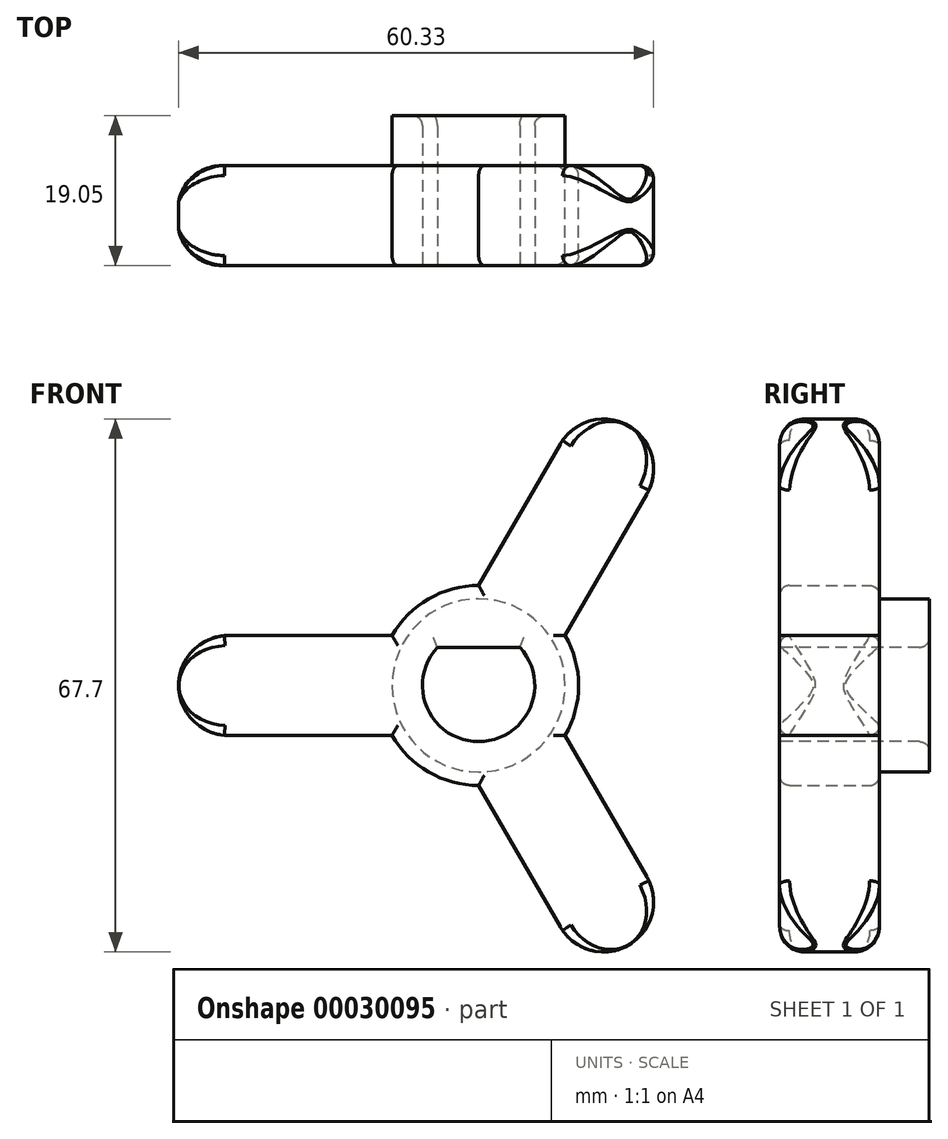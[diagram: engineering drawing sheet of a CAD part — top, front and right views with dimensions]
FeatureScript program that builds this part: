
annotation { "Feature Type Name" : "Feature", "Feature Type Description" : "" }
export const myFeature = defineFeature(function(context is Context, id is Id, definition is map)
    precondition{}
    {
        {
            var Q0;
            Q0=qCreatedBy(makeId("Front.planeOp"),FACE);
            var sketch = newSketch(context, id + "F0", { "sketchPlane" : qUnion([Q0])});
            skArc(sketch, "E0", {"start": v(-11, -6.35) * mm, "mid": v(-6.35, -11) * mm, "end": v(0, -12.7) * mm});
            skLineSegment(sketch, "E1", {"start": v(-12.7, 0) * mm, "end": v(-38.1, 0) * mm, "construction": true});
            skLineSegment(sketch, "E2", {"start": v(-11, 6.35) * mm, "end": v(-31.75, 6.35) * mm});
            skLineSegment(sketch, "E3", {"start": v(-38.1, 0) * mm, "end": v(-38.1, 0) * mm});
            skPoint(sketch, "E4.visualSharp", {"position": v(-38.1, 6.35) * mm});
            skArc(sketch, "E4.filletArc", {"start": v(-31.75, 6.35) * mm, "mid": v(-36.24, 4.5) * mm, "end": v(-38.1, 0) * mm});
            skLineSegment(sketch, "E5.MirrorCS", {"start": v(-11, -6.35) * mm, "end": v(-31.75, -6.35) * mm});
            skArc(sketch, "E6.MirrorCS", {"start": v(-31.75, -6.35) * mm, "mid": v(-36.24, -4.5) * mm, "end": v(-38.1, 0) * mm});
            skLineSegment(sketch, "E7.1.0", {"start": v(0, -12.7) * mm, "end": v(10.38, -30.67) * mm});
            skArc(sketch, "E7.1.1", {"start": v(10.38, -30.67) * mm, "mid": v(14.23, -33.63) * mm, "end": v(19.05, -33) * mm});
            skArc(sketch, "E7.1.2", {"start": v(21.37, -24.32) * mm, "mid": v(22, -29.14) * mm, "end": v(19.05, -33) * mm});
            skLineSegment(sketch, "E7.1.3", {"start": v(11, -6.35) * mm, "end": v(21.37, -24.32) * mm});
            skLineSegment(sketch, "E7.2.0", {"start": v(11, 6.35) * mm, "end": v(21.37, 24.32) * mm});
            skArc(sketch, "E7.2.1", {"start": v(21.37, 24.32) * mm, "mid": v(22, 29.14) * mm, "end": v(19.05, 33) * mm});
            skArc(sketch, "E7.2.2", {"start": v(10.38, 30.67) * mm, "mid": v(14.23, 33.63) * mm, "end": v(19.05, 33) * mm});
            skLineSegment(sketch, "E7.2.3", {"start": v(0, 12.7) * mm, "end": v(10.38, 30.67) * mm});
            skArc(sketch, "E8.trimOffspring", {"start": v(0, 12.7) * mm, "mid": v(-6.35, 11) * mm, "end": v(-11, 6.35) * mm});
            skArc(sketch, "E9.trimOffspring", {"start": v(11, -6.35) * mm, "mid": v(12.7, 0) * mm, "end": v(11, 6.35) * mm});
            skSolve(sketch);
        }
        {
            var Q0;
            Q0=makeQuery(id+"F0.imprint","IMPRINT",FACE,{"disambiguationData":[TD([[makeQuery(id+"F0.imprint","IMPRINT",EDGE,{"derivedFrom":sQuery(id+"F0.wireOp",EDGE,"E0")}),1.0]])]});
            extrude(context, id + "F1", {"entities" : qUnion([Q0]), "depth" : 19.05 * mm});
        }
        {
            var Q0;
            Q0=makeQuery(id+"F1.opExtrude","CAP_FACE",FACE,{"disambiguationData":[OSD([sQuery(id+"F0.wireOp",EDGE,"E0"),sQuery(id+"F0.wireOp",EDGE,"E2"),sQuery(id+"F0.wireOp",EDGE,"E4.filletArc"),sQuery(id+"F0.wireOp",EDGE,"E5.MirrorCS"),sQuery(id+"F0.wireOp",EDGE,"E6.MirrorCS"),sQuery(id+"F0.wireOp",EDGE,"E7.1.0"),sQuery(id+"F0.wireOp",EDGE,"E7.1.1"),sQuery(id+"F0.wireOp",EDGE,"E7.1.2"),sQuery(id+"F0.wireOp",EDGE,"E7.1.3"),sQuery(id+"F0.wireOp",EDGE,"E7.2.0"),sQuery(id+"F0.wireOp",EDGE,"E7.2.1"),sQuery(id+"F0.wireOp",EDGE,"E7.2.2"),sQuery(id+"F0.wireOp",EDGE,"E7.2.3"),sQuery(id+"F0.wireOp",EDGE,"E8.trimOffspring"),sQuery(id+"F0.wireOp",EDGE,"E9.trimOffspring")])],"isStart":false});
            var sketch = newSketch(context, id + "F2", { "sketchPlane" : qUnion([Q0])});
            skArc(sketch, "E10", {"start": v(-5.24, 4.85) * mm, "mid": v(0, -7.14) * mm, "end": v(5.24, 4.85) * mm});
            skLineSegment(sketch, "E11", {"start": v(-5.24, 4.85) * mm, "end": v(5.24, 4.85) * mm});
            skSolve(sketch);
        }
        {
            var Q0;
            Q0=makeQuery(id+"F2.imprint","IMPRINT",FACE,{"disambiguationData":[TD([[makeQuery(id+"F2.imprint","IMPRINT",EDGE,{"derivedFrom":sQuery(id+"F2.wireOp",EDGE,"E10")}),1.0]])]});
            extrude(context, id + "F3", {"entities" : qUnion([Q0]), "operationType" : NewBodyOperationType.REMOVE, "endBound" : BoundingType.THROUGH_ALL, "oppositeDirection" : true, "depth" : 25.4 * mm});
        }
        {
            var Q0;
            Q0=qCreatedBy(makeId("Top.planeOp"),FACE);
            var sketch = newSketch(context, id + "F4", { "sketchPlane" : qUnion([Q0])});
            skLineSegment(sketch, "E12", {"start": v(-38.18, -12.7) * mm, "end": v(-11, -12.7) * mm, "construction": true});
            skLineSegment(sketch, "E13", {"start": v(-11, -19.05) * mm, "end": v(-32.59, -19.05) * mm});
            skArc(sketch, "E14", {"start": v(-38.18, -12.7) * mm, "mid": v(-36.82, -17.14) * mm, "end": v(-32.59, -19.05) * mm});
            skLineSegment(sketch, "E15.MirrorCS", {"start": v(-11, -6.35) * mm, "end": v(-32.59, -6.35) * mm});
            skArc(sketch, "E16.MirrorCS", {"start": v(-38.18, -12.7) * mm, "mid": v(-36.82, -8.26) * mm, "end": v(-32.59, -6.35) * mm});
            skLineSegment(sketch, "E17", {"start": v(-11, -19.05) * mm, "end": v(-11, -6.35) * mm});
            skLineSegment(sketch, "E18", {"start": v(-11, -6.35) * mm, "end": v(-11, 0) * mm});
            skLineSegment(sketch, "E19", {"start": v(-11, 0) * mm, "end": v(-38.18, 0) * mm});
            skLineSegment(sketch, "E20", {"start": v(-38.18, 0) * mm, "end": v(-38.18, -12.7) * mm});
            skLineSegment(sketch, "E21.MirrorCS", {"start": v(-11, -19.05) * mm, "end": v(-11, -25.4) * mm});
            skLineSegment(sketch, "E22.MirrorCS", {"start": v(-38.18, -25.4) * mm, "end": v(-38.18, -12.7) * mm});
            skLineSegment(sketch, "E23.MirrorCS", {"start": v(-11, -25.4) * mm, "end": v(-38.18, -25.4) * mm});
            skSolve(sketch);
        }
        {
            var Q0;
            Q0=qCreatedBy(makeId("Right.planeOp"),FACE);
            var sketch = newSketch(context, id + "F5", { "sketchPlane" : qUnion([Q0])});
            skLineSegment(sketch, "E24", {"start": v(-63.5, 0) * mm, "end": v(63.5, 0) * mm, "construction": true});
            skSolve(sketch);
        }
        {
            var Q0;
            {var subQ4=sQuery(id+"F4.wireOp",EDGE,"E13");Q0=makeQuery(id+"F4.imprint","IMPRINT",FACE,{"disambiguationData":[TD([[makeQuery(id+"F4.imprint","IMPRINT",EDGE,{"derivedFrom":subQ4}),1.0]])]});}
            var Q1;
            {var subQ4=sQuery(id+"F4.wireOp",EDGE,"E15.MirrorCS");Q1=makeQuery(id+"F4.imprint","IMPRINT",FACE,{"disambiguationData":[TD([[makeQuery(id+"F4.imprint","IMPRINT",EDGE,{"derivedFrom":subQ4}),-1.0]])]});}
            var Q2;
            Q2 = qConstructionFilter(qBodyType(qCreatedBy(id + "F5" ,EDGE), BodyType.WIRE), ConstructionObject.NO);
            var Q3;
            Q3=sQuery(id+"F5.wireOp",EDGE,"E24");
            revolve(context, id + "F6", {"operationType" : NewBodyOperationType.REMOVE, "entities" : qUnion([Q0, Q1]), "surfaceEntities" : qUnion([Q2]), "axis" : qUnion([Q3]), "revolveType" : RevolveType.FULL, "oppositeDirection" : true});
        }
        {
            var Q0;
            Q0=makeQuery(id+"F6.boolean.opBoolean","COPY",EDGE,{"derivedFrom":makeQuery(id+"F6.opRevolve","SWEPT_EDGE",EDGE,{"disambiguationData":[OSD([sQuery(id+"F4.wireOp",EDGE,"E18"),sQuery(id+"F4.wireOp",EDGE,"E19")])]})});
            var Q1;
            Q1=makeQuery(id+"F3.boolean.opBoolean","INTERSECT",EDGE,{"derivedFrom":[makeQuery(id+"F1.opExtrude","CAP_FACE",FACE,{"disambiguationData":[OSD([sQuery(id+"F0.wireOp",EDGE,"E0"),sQuery(id+"F0.wireOp",EDGE,"E2"),sQuery(id+"F0.wireOp",EDGE,"E4.filletArc"),sQuery(id+"F0.wireOp",EDGE,"E5.MirrorCS"),sQuery(id+"F0.wireOp",EDGE,"E6.MirrorCS"),sQuery(id+"F0.wireOp",EDGE,"E7.1.0"),sQuery(id+"F0.wireOp",EDGE,"E7.1.1"),sQuery(id+"F0.wireOp",EDGE,"E7.1.2"),sQuery(id+"F0.wireOp",EDGE,"E7.1.3"),sQuery(id+"F0.wireOp",EDGE,"E7.2.0"),sQuery(id+"F0.wireOp",EDGE,"E7.2.1"),sQuery(id+"F0.wireOp",EDGE,"E7.2.2"),sQuery(id+"F0.wireOp",EDGE,"E7.2.3"),sQuery(id+"F0.wireOp",EDGE,"E8.trimOffspring"),sQuery(id+"F0.wireOp",EDGE,"E9.trimOffspring")])],"isStart":true}),makeQuery(id+"F3.opExtrude","SWEPT_FACE",FACE,{"disambiguationData":[OSD([sQuery(id+"F2.wireOp",EDGE,"E11")])]})]});
            var Q2;
            Q2=makeQuery(id+"F3.boolean.opBoolean","INTERSECT",EDGE,{"derivedFrom":[makeQuery(id+"F1.opExtrude","CAP_FACE",FACE,{"disambiguationData":[OSD([sQuery(id+"F0.wireOp",EDGE,"E0"),sQuery(id+"F0.wireOp",EDGE,"E2"),sQuery(id+"F0.wireOp",EDGE,"E4.filletArc"),sQuery(id+"F0.wireOp",EDGE,"E5.MirrorCS"),sQuery(id+"F0.wireOp",EDGE,"E6.MirrorCS"),sQuery(id+"F0.wireOp",EDGE,"E7.1.0"),sQuery(id+"F0.wireOp",EDGE,"E7.1.1"),sQuery(id+"F0.wireOp",EDGE,"E7.1.2"),sQuery(id+"F0.wireOp",EDGE,"E7.1.3"),sQuery(id+"F0.wireOp",EDGE,"E7.2.0"),sQuery(id+"F0.wireOp",EDGE,"E7.2.1"),sQuery(id+"F0.wireOp",EDGE,"E7.2.2"),sQuery(id+"F0.wireOp",EDGE,"E7.2.3"),sQuery(id+"F0.wireOp",EDGE,"E8.trimOffspring"),sQuery(id+"F0.wireOp",EDGE,"E9.trimOffspring")])],"isStart":true}),makeQuery(id+"F3.opExtrude","SWEPT_FACE",FACE,{"disambiguationData":[OSD([sQuery(id+"F2.wireOp",EDGE,"E10")])]})]});
            var Q3;
            Q3=makeQuery(id+"F3.boolean.opBoolean","COPY",EDGE,{"derivedFrom":makeQuery(id+"F3.opExtrude","CAP_EDGE",EDGE,{"disambiguationData":[OSD([sQuery(id+"F2.wireOp",EDGE,"E10")])],"isStart":true})});
            var Q4;
            Q4=makeQuery(id+"F1.opExtrude","CAP_EDGE",EDGE,{"disambiguationData":[OSD([sQuery(id+"F0.wireOp",EDGE,"E0")])],"isStart":false});
            var Q5;
            Q5=makeQuery(id+"F1.opExtrude","CAP_EDGE",EDGE,{"disambiguationData":[OSD([sQuery(id+"F0.wireOp",EDGE,"E5.MirrorCS")])],"isStart":false});
            var Q6;
            Q6=makeQuery(id+"F1.opExtrude","CAP_EDGE",EDGE,{"disambiguationData":[OSD([sQuery(id+"F0.wireOp",EDGE,"E7.1.0")])],"isStart":false});
            var Q7;
            Q7=makeQuery(id+"F1.opExtrude","CAP_EDGE",EDGE,{"disambiguationData":[OSD([sQuery(id+"F0.wireOp",EDGE,"E7.1.3")])],"isStart":false});
            var Q8;
            Q8=makeQuery(id+"F1.opExtrude","CAP_EDGE",EDGE,{"disambiguationData":[OSD([sQuery(id+"F0.wireOp",EDGE,"E9.trimOffspring")])],"isStart":false});
            var Q9;
            Q9=makeQuery(id+"F3.boolean.opBoolean","COPY",EDGE,{"derivedFrom":makeQuery(id+"F3.opExtrude","CAP_EDGE",EDGE,{"disambiguationData":[OSD([sQuery(id+"F2.wireOp",EDGE,"E11")])],"isStart":true})});
            var Q10;
            Q10=makeQuery(id+"F1.opExtrude","CAP_EDGE",EDGE,{"disambiguationData":[OSD([sQuery(id+"F0.wireOp",EDGE,"E8.trimOffspring")])],"isStart":false});
            var Q11;
            Q11=makeQuery(id+"F1.opExtrude","CAP_EDGE",EDGE,{"disambiguationData":[OSD([sQuery(id+"F0.wireOp",EDGE,"E2")])],"isStart":false});
            var Q12;
            Q12=makeQuery(id+"F1.opExtrude","CAP_EDGE",EDGE,{"disambiguationData":[OSD([sQuery(id+"F0.wireOp",EDGE,"E7.2.3")])],"isStart":false});
            var Q13;
            Q13=makeQuery(id+"F1.opExtrude","CAP_EDGE",EDGE,{"disambiguationData":[OSD([sQuery(id+"F0.wireOp",EDGE,"E7.2.0")])],"isStart":false});
            var Q14;
            Q14=makeQuery(id+"F6.boolean.opBoolean","INTERSECT",EDGE,{"derivedFrom":[makeQuery(id+"F1.opExtrude","SWEPT_FACE",FACE,{"disambiguationData":[OSD([sQuery(id+"F0.wireOp",EDGE,"E5.MirrorCS")])]}),makeQuery(id+"F6.opRevolve","SWEPT_FACE",FACE,{"disambiguationData":[OSD([sQuery(id+"F4.wireOp",EDGE,"E15.MirrorCS")])]})]});
            var Q15;
            Q15=makeQuery(id+"F6.boolean.opBoolean","INTERSECT",EDGE,{"derivedFrom":[makeQuery(id+"F1.opExtrude","SWEPT_FACE",FACE,{"disambiguationData":[OSD([sQuery(id+"F0.wireOp",EDGE,"E2")])]}),makeQuery(id+"F6.opRevolve","SWEPT_FACE",FACE,{"disambiguationData":[OSD([sQuery(id+"F4.wireOp",EDGE,"E15.MirrorCS")])]})]});
            var Q16;
            Q16=makeQuery(id+"F6.boolean.opBoolean","INTERSECT",EDGE,{"derivedFrom":[makeQuery(id+"F1.opExtrude","SWEPT_FACE",FACE,{"disambiguationData":[OSD([sQuery(id+"F0.wireOp",EDGE,"E0")])]}),makeQuery(id+"F6.opRevolve","SWEPT_FACE",FACE,{"disambiguationData":[OSD([sQuery(id+"F4.wireOp",EDGE,"E15.MirrorCS")])]})]});
            var Q17;
            Q17=makeQuery(id+"F6.boolean.opBoolean","INTERSECT",EDGE,{"derivedFrom":[makeQuery(id+"F1.opExtrude","SWEPT_FACE",FACE,{"disambiguationData":[OSD([sQuery(id+"F0.wireOp",EDGE,"E7.1.0")])]}),makeQuery(id+"F6.opRevolve","SWEPT_FACE",FACE,{"disambiguationData":[OSD([sQuery(id+"F4.wireOp",EDGE,"E15.MirrorCS")])]})]});
            var Q18;
            Q18=makeQuery(id+"F6.boolean.opBoolean","INTERSECT",EDGE,{"derivedFrom":[makeQuery(id+"F1.opExtrude","SWEPT_FACE",FACE,{"disambiguationData":[OSD([sQuery(id+"F0.wireOp",EDGE,"E7.1.3")])]}),makeQuery(id+"F6.opRevolve","SWEPT_FACE",FACE,{"disambiguationData":[OSD([sQuery(id+"F4.wireOp",EDGE,"E15.MirrorCS")])]})]});
            var Q19;
            Q19=makeQuery(id+"F6.boolean.opBoolean","INTERSECT",EDGE,{"derivedFrom":[makeQuery(id+"F1.opExtrude","SWEPT_FACE",FACE,{"disambiguationData":[OSD([sQuery(id+"F0.wireOp",EDGE,"E7.2.0")])]}),makeQuery(id+"F6.opRevolve","SWEPT_FACE",FACE,{"disambiguationData":[OSD([sQuery(id+"F4.wireOp",EDGE,"E15.MirrorCS")])]})]});
            var Q20;
            Q20=makeQuery(id+"F6.boolean.opBoolean","INTERSECT",EDGE,{"derivedFrom":[makeQuery(id+"F1.opExtrude","SWEPT_FACE",FACE,{"disambiguationData":[OSD([sQuery(id+"F0.wireOp",EDGE,"E9.trimOffspring")])]}),makeQuery(id+"F6.opRevolve","SWEPT_FACE",FACE,{"disambiguationData":[OSD([sQuery(id+"F4.wireOp",EDGE,"E15.MirrorCS")])]})]});
            var Q21;
            Q21=makeQuery(id+"F6.boolean.opBoolean","INTERSECT",EDGE,{"derivedFrom":[makeQuery(id+"F1.opExtrude","SWEPT_FACE",FACE,{"disambiguationData":[OSD([sQuery(id+"F0.wireOp",EDGE,"E7.2.3")])]}),makeQuery(id+"F6.opRevolve","SWEPT_FACE",FACE,{"disambiguationData":[OSD([sQuery(id+"F4.wireOp",EDGE,"E15.MirrorCS")])]})]});
            var Q22;
            Q22=makeQuery(id+"F6.boolean.opBoolean","INTERSECT",EDGE,{"derivedFrom":[makeQuery(id+"F1.opExtrude","SWEPT_FACE",FACE,{"disambiguationData":[OSD([sQuery(id+"F0.wireOp",EDGE,"E8.trimOffspring")])]}),makeQuery(id+"F6.opRevolve","SWEPT_FACE",FACE,{"disambiguationData":[OSD([sQuery(id+"F4.wireOp",EDGE,"E15.MirrorCS")])]})]});
            fillet(context, id + "F7", {"entities" : qUnion([Q0, Q1, Q2, Q3, Q4, Q5, Q6, Q7, Q8, Q9, Q10, Q11, Q12, Q13, Q14, Q15, Q16, Q17, Q18, Q19, Q20, Q21, Q22]), "radius" : 1.27 * mm, "tangentPropagation" : true, "allowEdgeOverflow" : false});
        }
    });
